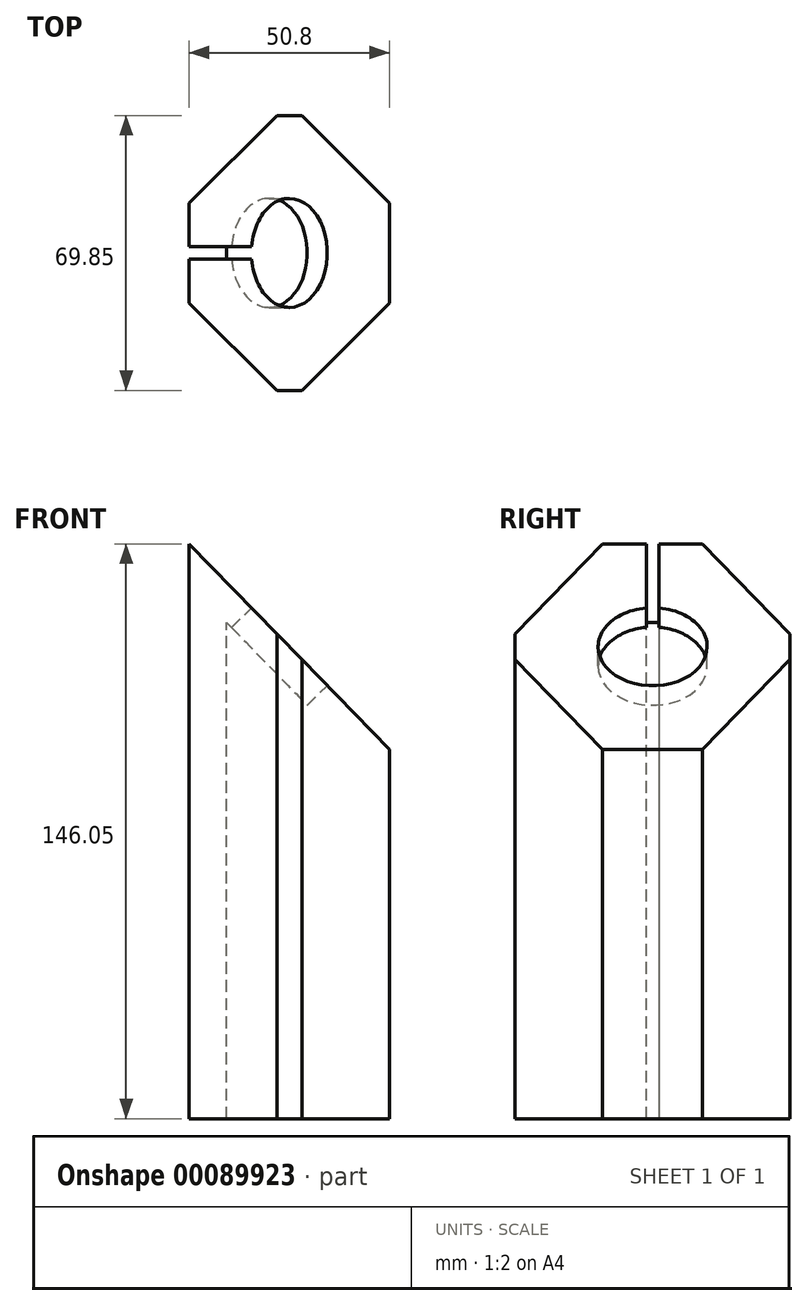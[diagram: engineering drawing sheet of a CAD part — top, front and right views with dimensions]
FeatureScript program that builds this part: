
annotation { "Feature Type Name" : "Feature", "Feature Type Description" : "" }
export const myFeature = defineFeature(function(context is Context, id is Id, definition is map)
    precondition{}
    {
        {
            var Q0;
            Q0=qCreatedBy(makeId("Top.planeOp"),FACE);
            var sketch = newSketch(context, id + "F0", { "sketchPlane" : qUnion([Q0])});
            skLineSegment(sketch, "E0.bottom", {"start": v(0, 0) * mm, "end": v(50.8, 0) * mm});
            skLineSegment(sketch, "E0.top", {"start": v(0, 69.85) * mm, "end": v(50.8, 69.85) * mm});
            skLineSegment(sketch, "E0.left", {"start": v(0, 0) * mm, "end": v(0, 69.85) * mm});
            skLineSegment(sketch, "E0.right", {"start": v(50.8, 0) * mm, "end": v(50.8, 69.85) * mm});
            skSolve(sketch);
        }
        {
            var Q0;
            Q0 = qSketchRegion(id + "F0", true);
            extrude(context, id + "F1", {"entities" : qUnion([Q0]), "depth" : 146.05 * mm});
        }
        {
            var Q0;
            Q0=makeQuery(id+"F1.opExtrude","SWEPT_FACE",FACE,{"disambiguationData":[OSD([sQuery(id+"F0.wireOp",EDGE,"E0.bottom")])]});
            var sketch = newSketch(context, id + "F2", { "sketchPlane" : qUnion([Q0])});
            skLineSegment(sketch, "E1", {"start": v(0, 146.05) * mm, "end": v(50.8, 93.77) * mm});
            skSolve(sketch);
        }
        {
            var Q0;
            Q0 = qSketchRegion(id + "F2", true);
            var Q1;
            {var subQ0=sQuery(id+"F2.wireOp",EDGE,"E1");Q1=makeQuery(id+"F2.imprint","IMPRINT",FACE,{"disambiguationData":[TD([[makeQuery(id+"F2.imprint","IMPRINT",EDGE,{"derivedFrom":subQ0}),1.0]])]});}
            extrude(context, id + "F3", {"entities" : qUnion([Q0, Q1]), "operationType" : NewBodyOperationType.REMOVE, "endBound" : BoundingType.THROUGH_ALL, "oppositeDirection" : true, "depth" : 25.4 * mm});
        }
        {
            var Q0;
            Q0=makeQuery(id+"F3.boolean.opBoolean","COPY",FACE,{"derivedFrom":makeQuery(id+"F3.opExtrude","SWEPT_FACE",FACE,{"disambiguationData":[OSD([sQuery(id+"F2.wireOp",EDGE,"E1")])]})});
            var sketch = newSketch(context, id + "F4", { "sketchPlane" : qUnion([Q0])});
            skCircle(sketch, "E2", {"center": v(34.93, 68.3) * mm, "radius": 13.84 * mm});
            skPoint(sketch, "E2.centerSnap0", {"position": v(0, 68.3) * mm});
            skPoint(sketch, "E2.centerSnap1", {"position": v(34.93, 104.74) * mm});
            skSolve(sketch);
        }
        {
            var Q0;
            Q0 = qSketchRegion(id + "F4", true);
            extrude(context, id + "F5", {"entities" : qUnion([Q0]), "operationType" : NewBodyOperationType.REMOVE, "oppositeDirection" : true, "depth" : 7.11 * mm});
        }
        {
            var Q0;
            Q0=makeQuery(id+"F1.opExtrude","SWEPT_EDGE",EDGE,{"disambiguationData":[OSD([sQuery(id+"F0.wireOp",EDGE,"E0.bottom"),sQuery(id+"F0.wireOp",EDGE,"E0.right")])]});
            var Q1;
            Q1=makeQuery(id+"F1.opExtrude","SWEPT_EDGE",EDGE,{"disambiguationData":[OSD([sQuery(id+"F0.wireOp",EDGE,"E0.top"),sQuery(id+"F0.wireOp",EDGE,"E0.right")])]});
            var Q2;
            Q2=makeQuery(id+"F1.opExtrude","SWEPT_EDGE",EDGE,{"disambiguationData":[OSD([sQuery(id+"F0.wireOp",EDGE,"E0.top"),sQuery(id+"F0.wireOp",EDGE,"E0.left")])]});
            var Q3;
            Q3=makeQuery(id+"F1.opExtrude","SWEPT_EDGE",EDGE,{"disambiguationData":[OSD([sQuery(id+"F0.wireOp",EDGE,"E0.bottom"),sQuery(id+"F0.wireOp",EDGE,"E0.left")])]});
            chamfer(context, id + "F6", {"entities" : qUnion([Q0, Q1, Q2, Q3]), "width" : 22.22 * mm, "tangentPropagation" : true});
        }
        {
            var Q0;
            Q0=makeQuery(id+"F1.opExtrude","SWEPT_FACE",FACE,{"disambiguationData":[OSD([sQuery(id+"F0.wireOp",EDGE,"E0.left")])]});
            var sketch = newSketch(context, id + "F7", { "sketchPlane" : qUnion([Q0])});
            skLineSegment(sketch, "E3", {"start": v(-36.51, 146.05) * mm, "end": v(-36.51, 0) * mm});
            skLineSegment(sketch, "E4", {"start": v(-36.51, 0) * mm, "end": v(-33.34, 0) * mm});
            skLineSegment(sketch, "E5", {"start": v(-33.34, 0) * mm, "end": v(-33.34, 146.05) * mm});
            skLineSegment(sketch, "E6", {"start": v(-33.34, 146.05) * mm, "end": v(-36.51, 146.05) * mm});
            skSolve(sketch);
        }
        {
            var Q0;
            Q0 = qSketchRegion(id + "F7", true);
            extrude(context, id + "F8", {"entities" : qUnion([Q0]), "operationType" : NewBodyOperationType.REMOVE, "oppositeDirection" : true, "depth" : 9.52 * mm});
        }
        {
            var Q0;
            Q0=makeQuery(id+"F3.boolean.opBoolean","COPY",FACE,{"derivedFrom":makeQuery(id+"F3.opExtrude","SWEPT_FACE",FACE,{"disambiguationData":[OSD([sQuery(id+"F2.wireOp",EDGE,"E1")])]})});
            var sketch = newSketch(context, id + "F9", { "sketchPlane" : qUnion([Q0])});
            skLineSegment(sketch, "E7", {"start": v(33.34, 91.08) * mm, "end": v(33.34, 82.05) * mm});
            skLineSegment(sketch, "E8", {"start": v(36.51, 91.08) * mm, "end": v(36.51, 82.05) * mm});
            skSolve(sketch);
        }
        {
            var Q0;
            Q0 = qSketchRegion(id + "F9", true);
            var Q1;
            {var subQ0=sQuery(id+"F9.wireOp",EDGE,"E7");Q1=makeQuery(id+"F9.imprint","IMPRINT",FACE,{"disambiguationData":[TD([[makeQuery(id+"F9.imprint","IMPRINT",EDGE,{"derivedFrom":subQ0}),1.0]])]});}
            extrude(context, id + "F10", {"entities" : qUnion([Q0, Q1]), "operationType" : NewBodyOperationType.REMOVE, "oppositeDirection" : true, "depth" : 7.11 * mm});
        }
    });
